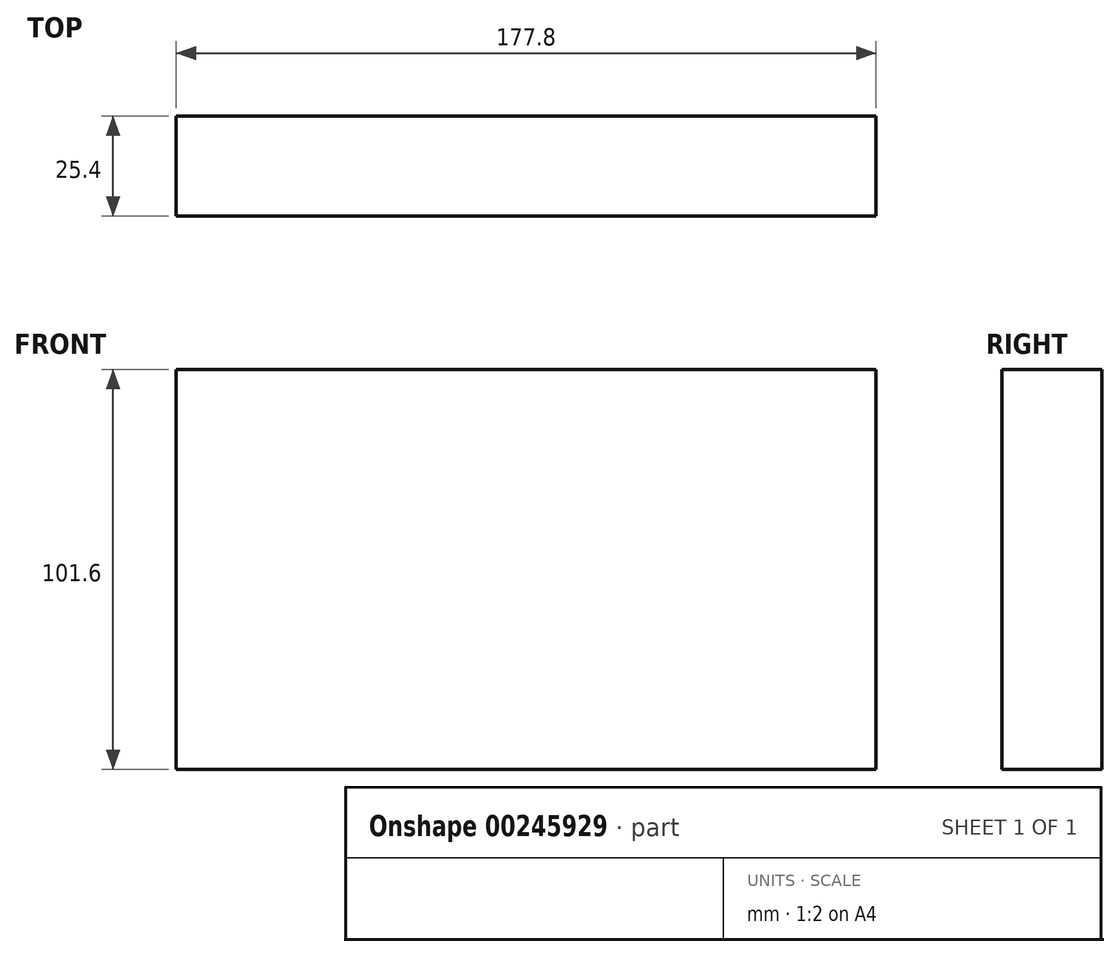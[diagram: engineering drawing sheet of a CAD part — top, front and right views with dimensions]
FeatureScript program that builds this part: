
annotation { "Feature Type Name" : "Feature", "Feature Type Description" : "" }
export const myFeature = defineFeature(function(context is Context, id is Id, definition is map)
    precondition{}
    {
        {
            var Q0;
            Q0=qCreatedBy(makeId("Front.planeOp"),FACE);
            var sketch = newSketch(context, id + "F0", { "sketchPlane" : qUnion([Q0])});
            skLineSegment(sketch, "E0", {"start": v(-100.27, 0) * mm, "end": v(77.53, 0) * mm});
            skLineSegment(sketch, "E1", {"start": v(-100.27, 0) * mm, "end": v(-100.27, 101.6) * mm});
            skLineSegment(sketch, "E2", {"start": v(77.53, 0) * mm, "end": v(77.53, 101.6) * mm});
            skLineSegment(sketch, "E3", {"start": v(77.53, 101.6) * mm, "end": v(-100.27, 101.6) * mm});
            skSolve(sketch);
        }
        {
            var Q0;
            Q0=makeQuery(id+"F0.imprint","IMPRINT",FACE,{"disambiguationData":[TD([[makeQuery(id+"F0.imprint","IMPRINT",EDGE,{"derivedFrom":sQuery(id+"F0.wireOp",EDGE,"E0")}),1.0]])]});
            extrude(context, id + "F1", {"entities" : qUnion([Q0]), "depth" : 25.4 * mm});
        }
    });
